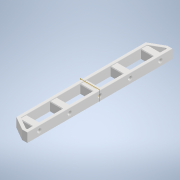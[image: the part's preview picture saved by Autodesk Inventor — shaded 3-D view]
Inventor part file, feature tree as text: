
AUTODESK INVENTOR PART (.ipt)
format: ipt  version: 2022 (Build 260153000, 153)  size: 224,768 bytes
history: native  units: in
note: dims shown in document units (in); Inventor stores cm internally (conversion verified against a paired STEP export)
features: extrude x4, sketch x4, chamfer x3, projected_geometry x2, plane x1, mirror x1, shell x1, pattern_linear x1, fillet x1
ambient origin geometry x8: Origin, YZ Plane, XZ Plane, XY Plane, X Axis, Y Axis, Z Axis, Center Point
bodies: Body1 (feature_tree)
feature tree (18):
  extrude  "Extrusion2"  Depth=1.2402in
  plane  "Work Plane1"
  extrude  "Extrusion3"  TaperAngle=0.0deg  [1 undecoded]
  mirror  "Mirror1"
  shell  "Shell1"  Thickness=30.0deg
  extrude  "Extrusion4"  TaperAngle=0.0deg  [1 undecoded]
  extrude  "Extrusion5"  Depth=0.1969in
  chamfer  "Chamfer1"  Distance=8.4105in
  chamfer  "Chamfer2"  Distance=0.4724in
  chamfer  "Chamfer3"  Distance=0.5906in
  pattern_linear  "Rectangular Pattern1"  Spacing1=0.2953in  [1 undecoded]
  fillet  "Fillet1"  Radius=0.0394in
  sketch  "Sketch2"  dims[d4=1.2402in d5=9.8425in]
  sketch  "Sketch3"  dims[d6=0.5906in d7=0.0in d8=30.0deg]
  projected_geometry  "Projected Loop1"
  sketch  "Sketch5"  dims[d9=0.5906in d10=0.0in]
  projected_geometry  "Projected Loop2"
  sketch  "Sketch7"  dims[d11=0.1969in d12=0.1969in d15=8.4105in d17=0.4724in d18=0.5906in d19=0.2953in d20=0.0394in d21=0.0in d22=0.0in d23=1.9685in d25=1.9685in d26=0.2165in d27=0.5512in d28=0.2756in d29=0.4724in d30=0.2362in d31=0.0in d32=0.0in d33=0.1181in d34=0.0787in d35=45.0deg d36=0.0394in d37=0.0787in d38=45.0deg d39=0.0197in d41=0.0394in d42=0.0787in d43=45.0deg]
note: 3 required parameter values undecoded (feature->parameter linkage not recoverable at this tier; creation-order binding heuristic only, values carry confidence <= 0.55)
